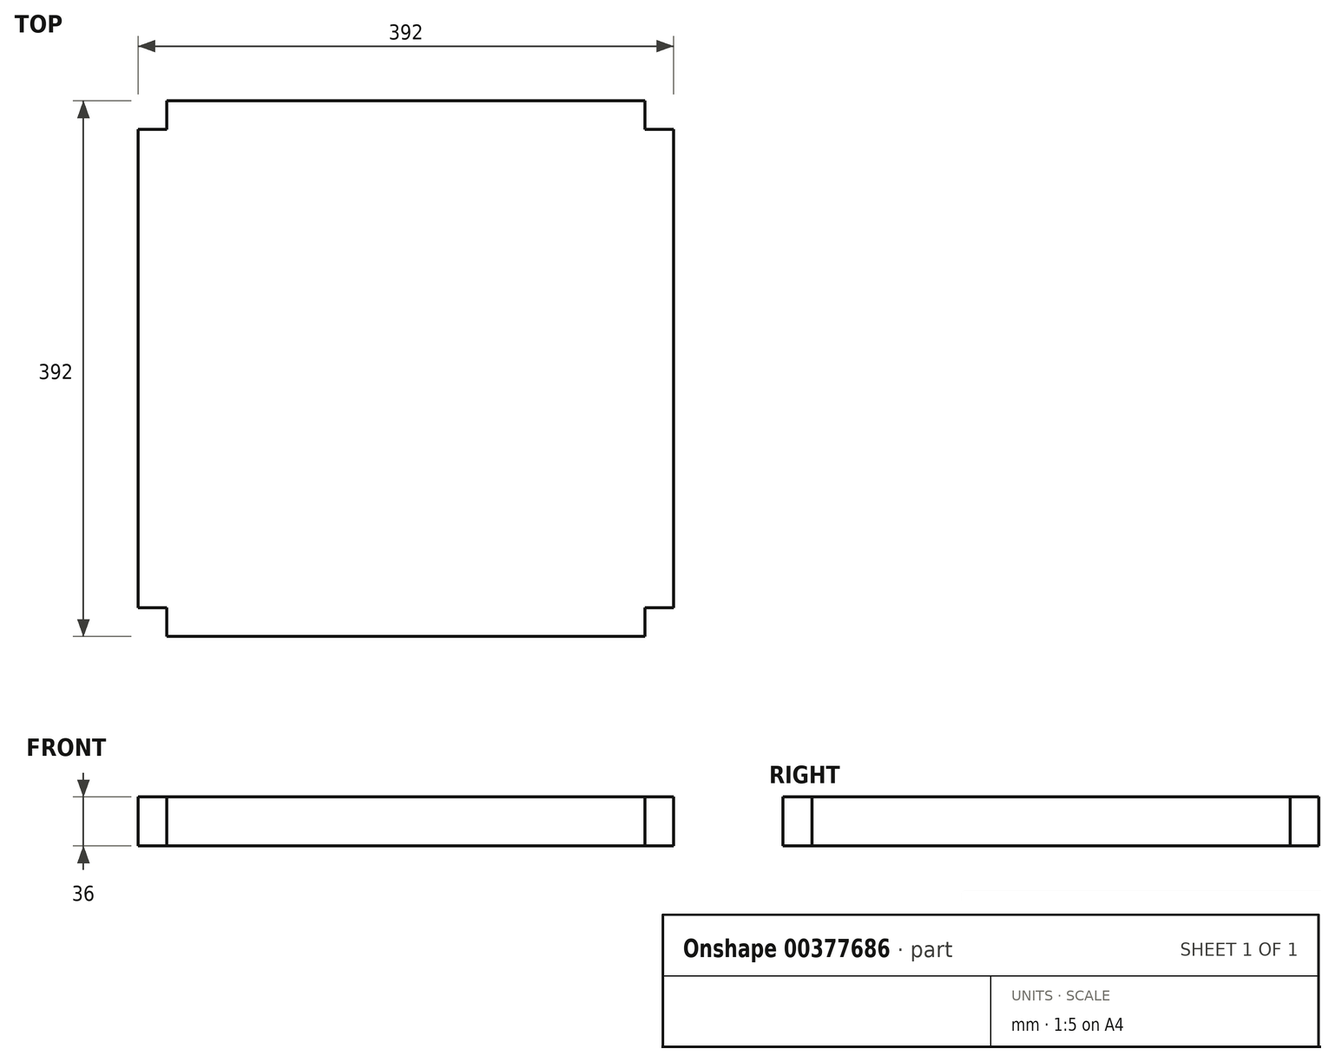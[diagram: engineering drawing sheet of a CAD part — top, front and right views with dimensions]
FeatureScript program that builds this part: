
annotation { "Feature Type Name" : "Feature", "Feature Type Description" : "" }
export const myFeature = defineFeature(function(context is Context, id is Id, definition is map)
    precondition{}
    {
        {
            var Q0;
            Q0=qCreatedBy(makeId("Top.planeOp"),FACE);
            var sketch = newSketch(context, id + "F0", { "sketchPlane" : qUnion([Q0])});
            skLineSegment(sketch, "E0.bottom", {"start": v(21, 0) * mm, "end": v(371, 0) * mm});
            skLineSegment(sketch, "E0.top", {"start": v(21, 392) * mm, "end": v(371, 392) * mm});
            skLineSegment(sketch, "E0.left", {"start": v(0, 21) * mm, "end": v(0, 371) * mm});
            skLineSegment(sketch, "E0.right", {"start": v(392, 21) * mm, "end": v(392, 371) * mm});
            skLineSegment(sketch, "E1.top", {"start": v(0, 371) * mm, "end": v(21, 371) * mm});
            skLineSegment(sketch, "E1.right", {"start": v(21, 392) * mm, "end": v(21, 371) * mm});
            skPoint(sketch, "E2.endSnap0", {"position": v(0, 196) * mm});
            skLineSegment(sketch, "E3.MirrorCS", {"start": v(371, 392) * mm, "end": v(371, 371) * mm});
            skLineSegment(sketch, "E4.MirrorCS", {"start": v(392, 371) * mm, "end": v(371, 371) * mm});
            skLineSegment(sketch, "E5.MirrorCS", {"start": v(0, 21) * mm, "end": v(21, 21) * mm});
            skLineSegment(sketch, "E6.MirrorCS", {"start": v(21, 0) * mm, "end": v(21, 21) * mm});
            skLineSegment(sketch, "E7.MirrorCS", {"start": v(392, 21) * mm, "end": v(371, 21) * mm});
            skLineSegment(sketch, "E8.MirrorCS", {"start": v(371, 0) * mm, "end": v(371, 21) * mm});
            skPoint(sketch, "E9.orphan", {"position": v(0, 392) * mm});
            skPoint(sketch, "E10.orphan", {"position": v(0, 0) * mm});
            skSolve(sketch);
        }
        {
            var Q0;
            Q0=makeQuery(id+"F0.imprint","IMPRINT",FACE,{"disambiguationData":[TD([[makeQuery(id+"F0.imprint","IMPRINT",EDGE,{"derivedFrom":sQuery(id+"F0.wireOp",EDGE,"E0.bottom")}),1.0]])]});
            extrude(context, id + "F1", {"entities" : qUnion([Q0]), "depth" : (2 * 18) * mm});
        }
    });
